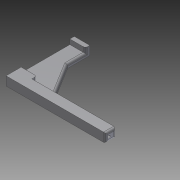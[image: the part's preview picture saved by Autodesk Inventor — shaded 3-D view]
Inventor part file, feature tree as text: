
AUTODESK INVENTOR PART (.ipt)
format: ipt  version: 2011 (Build 150239000, 239)  size: 129,536 bytes
history: native  units: mm
features: sketch x3, extrude x2, fillet x2, other x1, hole x1
ambient origin geometry x8: Origin, YZ Plane, XZ Plane, XY Plane, X Axis, Y Axis, Z Axis, Center Point
feature tree (9):
  other  "Sólido1"
  extrude  "Extrusión1"  Depth=7.0mm
  extrude  "Extrusión2"  Depth=45.0mm
  fillet  "Empalme1"  Radius=4.6mm
  fillet  "Empalme2"  Radius=28.0mm
  hole  "Hole1"  [1 undecoded]
  sketch  "Boceto1"  dims[d0=30.8mm d1=7.0mm]
  sketch  "Boceto2"  dims[d2=10.0mm d3=45.0mm d4=4.6mm d5=28.0mm]
  sketch  "Boceto3"  dims[d6=1.8mm d7=0.0mm d8=10.0mm d12=2.2mm d13=0.0mm d14=6.8mm d16=1.0mm d18=2.0mm d19=1.0mm d20=0.5mm d21=1.0mm d22=1.0mm d23=6.0mm d24=4.0mm d25=2.0mm d26=90.0deg d27=3.0mm d28=0.0mm]
note: 1 required parameter value undecoded (feature->parameter linkage not recoverable at this tier; creation-order binding heuristic only, values carry confidence <= 0.55)
